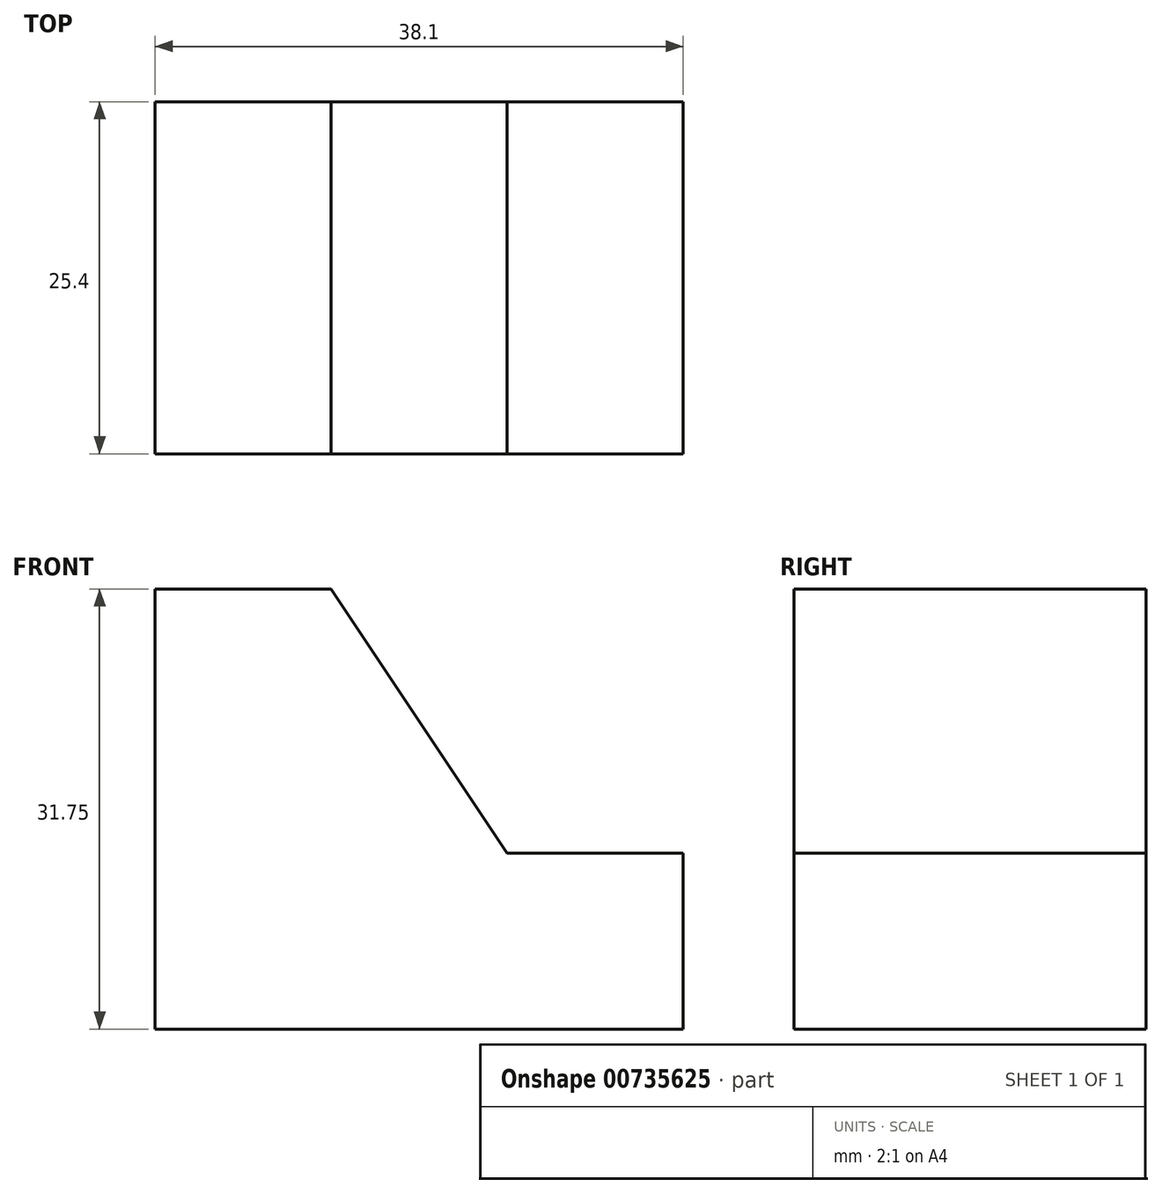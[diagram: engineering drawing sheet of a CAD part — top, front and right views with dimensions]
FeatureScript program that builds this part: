
annotation { "Feature Type Name" : "Feature", "Feature Type Description" : "" }
export const myFeature = defineFeature(function(context is Context, id is Id, definition is map)
    precondition{}
    {
        {
            var Q0;
            Q0=qCreatedBy(makeId("Front.planeOp"),FACE);
            var sketch = newSketch(context, id + "F0", { "sketchPlane" : qUnion([Q0])});
            skLineSegment(sketch, "E0.bottom", {"start": v(0, 0) * mm, "end": v(38.1, 0) * mm});
            skLineSegment(sketch, "E0.top", {"start": v(0, 31.75) * mm, "end": v(38.1, 31.75) * mm});
            skLineSegment(sketch, "E0.left", {"start": v(0, 0) * mm, "end": v(0, 31.75) * mm});
            skLineSegment(sketch, "E0.right", {"start": v(38.1, 0) * mm, "end": v(38.1, 31.75) * mm});
            skSolve(sketch);
        }
        {
            var Q0;
            Q0 = qSketchRegion(id + "F0", true);
            extrude(context, id + "F1", {"entities" : qUnion([Q0]), "depth" : 25.4 * mm, "offsetDistance" : 25.4 * mm});
        }
        {
            var Q0;
            Q0=makeQuery(id+"F1.opExtrude","CAP_FACE",FACE,{"disambiguationData":[OSD([sQuery(id+"F0.wireOp",EDGE,"E0.bottom"),sQuery(id+"F0.wireOp",EDGE,"E0.top"),sQuery(id+"F0.wireOp",EDGE,"E0.left"),sQuery(id+"F0.wireOp",EDGE,"E0.right")])],"isStart":false});
            var sketch = newSketch(context, id + "F2", { "sketchPlane" : qUnion([Q0])});
            skLineSegment(sketch, "E1", {"start": v(12.7, 31.75) * mm, "end": v(38.1, 31.75) * mm});
            skLineSegment(sketch, "E2", {"start": v(38.1, 31.75) * mm, "end": v(38.1, 12.7) * mm});
            skLineSegment(sketch, "E3", {"start": v(38.1, 12.7) * mm, "end": v(25.4, 12.7) * mm});
            skLineSegment(sketch, "E4", {"start": v(12.7, 31.75) * mm, "end": v(25.4, 12.7) * mm});
            skSolve(sketch);
        }
        {
            var Q0;
            Q0=makeQuery(id+"F2.imprint","IMPRINT",FACE,{"disambiguationData":[TD([[makeQuery(id+"F2.imprint","IMPRINT",EDGE,{"derivedFrom":sQuery(id+"F2.wireOp",EDGE,"E1")}),-1.0]])]});
            extrude(context, id + "F3", {"entities" : qUnion([Q0]), "operationType" : NewBodyOperationType.REMOVE, "oppositeDirection" : true, "depth" : 25.4 * mm, "offsetDistance" : 25.4 * mm});
        }
    });
